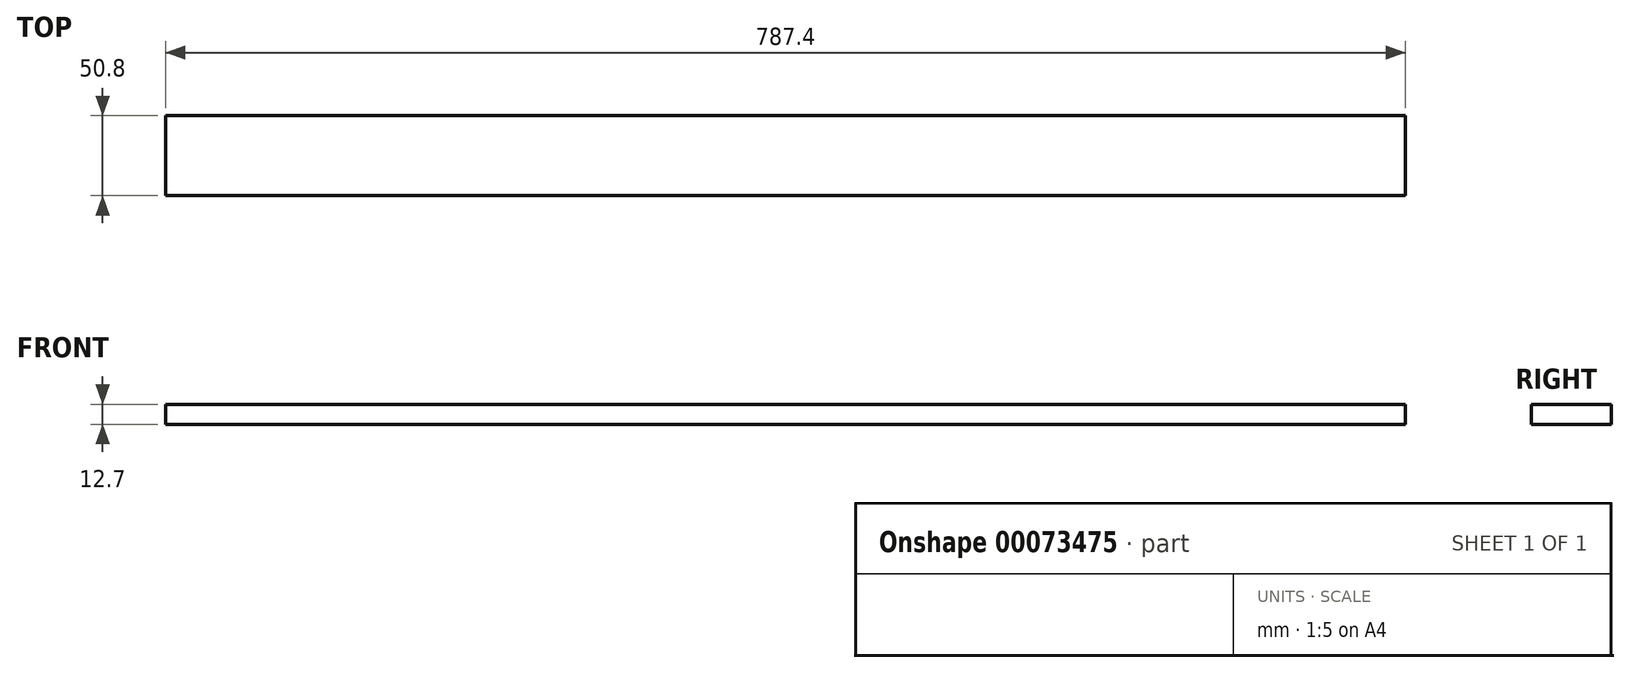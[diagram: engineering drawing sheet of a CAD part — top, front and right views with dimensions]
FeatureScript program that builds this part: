
annotation { "Feature Type Name" : "Feature", "Feature Type Description" : "" }
export const myFeature = defineFeature(function(context is Context, id is Id, definition is map)
    precondition{}
    {
        {
            var Q0;
            Q0=qCreatedBy(makeId("Top.planeOp"),FACE);
            var sketch = newSketch(context, id + "F0", { "sketchPlane" : qUnion([Q0])});
            skLineSegment(sketch, "E0.bottom", {"start": v(-401.22, -127.05) * mm, "end": v(386.18, -127.05) * mm});
            skLineSegment(sketch, "E0.top", {"start": v(-401.22, -76.25) * mm, "end": v(386.18, -76.25) * mm});
            skLineSegment(sketch, "E0.left", {"start": v(-401.22, -127.05) * mm, "end": v(-401.22, -76.25) * mm});
            skLineSegment(sketch, "E0.right", {"start": v(386.18, -127.05) * mm, "end": v(386.18, -76.25) * mm});
            skSolve(sketch);
        }
        {
            var Q0;
            Q0=makeQuery(id+"F0.imprint","IMPRINT",FACE,{"disambiguationData":[TD([[makeQuery(id+"F0.imprint","IMPRINT",EDGE,{"derivedFrom":sQuery(id+"F0.wireOp",EDGE,"E0.bottom")}),1.0]])]});
            extrude(context, id + "F1", {"entities" : qUnion([Q0]), "depth" : 12.7 * mm});
        }
    });
